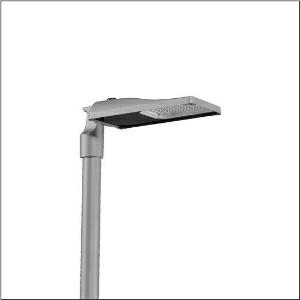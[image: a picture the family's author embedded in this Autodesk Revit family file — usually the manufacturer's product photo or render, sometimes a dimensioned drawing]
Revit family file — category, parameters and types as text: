
# Revit family: streetlight_sl_31_mini___st1_0a_5xh6d3as08ga_7bf7
name_source: partatom
category: Lighting Fixtures
units: mm (PartAtom-declared; Revit-internal decimal feet)

## family parameters
Cut with Voids When Loaded = No
Host = Face
Light Source = No
Part Type = Normal
Room Calculation Point = No
Round Connector Dimension = Use Diameter
Shared = No

## types (1)
- --- (1 x LED, 5880 lm, 39.3 W, 3000K)
    Apparent Load = 39 VA
    CIE Flux Codes = 37 72 97 100 100
    Color Rendering = 70
    Color Temperature = 3000K
    Default Elevation = 1800 mm
    Description = Streetlight SL 31 mini D4i mast luminaire for post-top, side-entry; light control with lens of PMMA; light distribution: ST1.0a, direct asymmetric distribution, for standard-compliant lighting for roads and squares; LED: luminous flux: 5.880lm, light colour: 730, colour temperature: 3000K; luminous efficacy: 149,6lm/W; control: pre-setting: logarithmic dimming characteristic, flexible luminous flux parameterisation, time-dependent luminous flux control, constant luminous flux control, power reduction, intelligent temperature release in ECG and LED module, overheat protection; luminaire housing, of diecast aluminium, SITECO metallic grey (DB 702S), corrosivity category C5 high according to DIN EN ISO 12944; cover of toughened safety glass, transparent, opened without tools; mast flange of diecast aluminium, SITECO metallic grey (DB 702S), spigot size: 76/60mm, mast flange included unmounted; cable length: 6,5m, connection cable pre-assembled; mains connection: 220..240V, AC, 50/60Hz; power consumption (at start of service life): 39,3W / (at end of service life): 40,7W / (with reduced operation 50%): 18,1W; protection rating (complete): IP66; insulation class (complete): insulation class II (safety insulation); impact resistance: IK10; certification: CE, ENEC, ENEC+, VDE, UKCA, ZD4i; permissible operating ambient temperature for outdoor applications: -40..+50°C; packaging unit: 1 piece

Light Distribution: ST1.0a
    Height = 76 mm
    Lamp = 1 x LED
    Lamp Light Flux = 5880 lm
    Lamp Power = 39.3 W
    Lamp count = 1
    Length = 547 mm
    Luminous efficacy = 150 lm/W
    Manufacturer = Siteco
    ModVariant = No
    Model = 5XH6D3AS08GA
    Number of Poles = 1
    OnlyDefault = Yes
    Power Factor = 1
    Product Name = Streetlight SL 31 mini | ST1.0a
    Product group = mast luminaire | pylon top
    ProductGroupID = 6100
    Protection Class = Protection class II
    Protection Degree = IP 66
    RLX_Detail_Level = 1
    RLX_Emergency_Light_Flux = 0 lm
    RLX_Emergency_Type = 0
    RLX_Emergency_Type_DB = No
    RlxData = <blob elided: 39561 chars, md5=313669c5>
    Socket = socket
    Standby Power = 0 W
    System Light Flux = 5880 lm
    System Power = 39 W
    Type Comments = factory setting: luminous flux: 100 % | dim-lin: 254 | 798 mA
    Type Image = l_1300330.jpg
    URL = http://relux.com
    VarID = @adj_060665
    Voltage = 0 V
    Weight = 0.00 kg
    Width = 265 mm

## geometry (parser evidence)
native form markers: Blend x4, Sweep x9
no freeform markers — native parametric forms only
